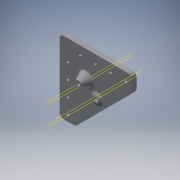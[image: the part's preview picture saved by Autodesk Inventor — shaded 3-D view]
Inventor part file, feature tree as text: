
AUTODESK INVENTOR PART (.ipt)
format: ipt  version: 2018 (Build 220112000, 112)  size: 210,432 bytes
history: native  units: in
note: dims shown in document units (in); Inventor stores cm internally (conversion verified against a paired STEP export)
features: sketch x7, extrude x5, plane x4, revolve x2, fillet x2, projected_geometry x2
ambient origin geometry x8: Origin, YZ Plane, XZ Plane, XY Plane, X Axis, Y Axis, Z Axis, Center Point
bodies: Solid1 (feature_tree)
feature tree (22):
  extrude  "Extrusion1"  Depth=0.7874in
  extrude  "Extrusion2"  Depth=3.5433in
  plane  "Work Plane2"
  revolve  "Revolution1"  [1 undecoded]
  extrude  "Extrusion3"  Depth=0.5512in
  extrude  "Extrusion4"  [1 undecoded]
  fillet  "Fillet1"  Radius=0.3543in
  extrude  "Extrusion5"  TaperAngle=90.0deg  [1 undecoded]
  plane  "Work Plane4"
  revolve  "Revolution2"  [1 undecoded]
  fillet  "Fillet2"  Radius=0.1654in
  sketch  "Sketch1"  dims[d0=0.7874in d1=0.7874in]
  sketch  "Sketch2"  dims[d2=3.5433in d3=3.5433in]
  plane  "Work Plane1"
  sketch  "Sketch3"  dims[d4=0.2362in d5=0.0in d6=0.1969in]
  sketch  "Sketch4"  dims[d7=1.2992in d8=0.5512in]
  projected_geometry  "Projected Loop1"
  sketch  "Sketch5"  dims[d9=0.2362in d10=0.0in d11=-0.0984in d12=0.3543in]
  sketch  "Sketch7"  dims[d13=0.3937in d14=90.0deg]
  plane  "Work Plane3"
  sketch  "Sketch8"  dims[d15=0.2362in d16=0.0in d17=0.1575in d18=0.1654in d19=0.315in d20=0.748in d21=0.748in d22=0.748in d23=0.315in d24=0.748in d25=0.748in d26=0.748in d27=0.2362in d28=0.0in d29=0.0787in d30=0.3543in d32=0.3543in d33=0.1969in d34=0.0in d35=0.0984in d36=0.1969in d37=0.0591in d38=0.0787in d39=90.0deg d40=0.1969in]
  projected_geometry  "Projected Loop2"
note: 4 required parameter values undecoded (feature->parameter linkage not recoverable at this tier; creation-order binding heuristic only, values carry confidence <= 0.55)